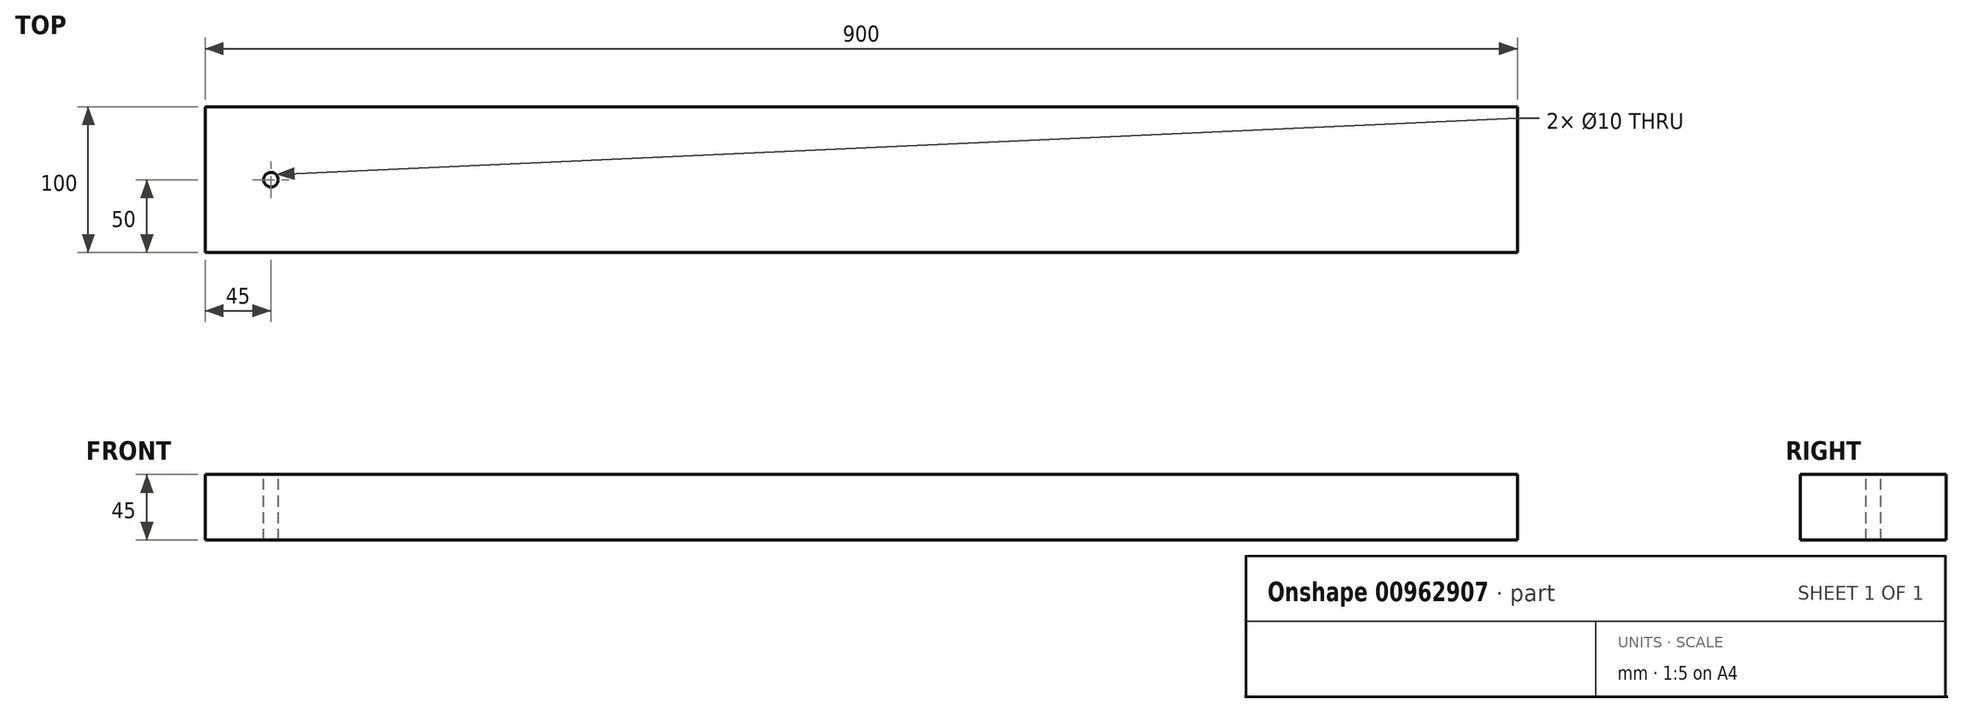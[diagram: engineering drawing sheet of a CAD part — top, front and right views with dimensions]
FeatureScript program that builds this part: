
annotation { "Feature Type Name" : "Feature", "Feature Type Description" : "" }
export const myFeature = defineFeature(function(context is Context, id is Id, definition is map)
    precondition{}
    {
        {
            var Q0;
            Q0=qCreatedBy(makeId("Top.planeOp"),FACE);
            var sketch = newSketch(context, id + "F0", { "sketchPlane" : qUnion([Q0])});
            skLineSegment(sketch, "E0.bottom", {"start": v(-450, 50) * mm, "end": v(450, 50) * mm});
            skLineSegment(sketch, "E0.top", {"start": v(-450, -50) * mm, "end": v(450, -50) * mm});
            skLineSegment(sketch, "E0.left", {"start": v(-450, 50) * mm, "end": v(-450, -50) * mm});
            skLineSegment(sketch, "E0.right", {"start": v(450, 50) * mm, "end": v(450, -50) * mm});
            skPoint(sketch, "E0.middle", {"position": v(0, 0) * mm});
            skSolve(sketch);
        }
        {
            var Q0;
            Q0 = qSketchRegion(id + "F0", true);
            extrude(context, id + "F1", {"entities" : qUnion([Q0]), "depth" : 45 * mm, "offsetDistance" : 25 * mm});
        }
        {
            var Q0;
            Q0=makeQuery(id+"F1.opExtrude","CAP_FACE",FACE,{"disambiguationData":[OSD([sQuery(id+"F0.wireOp",EDGE,"E0.bottom"),sQuery(id+"F0.wireOp",EDGE,"E0.top"),sQuery(id+"F0.wireOp",EDGE,"E0.left"),sQuery(id+"F0.wireOp",EDGE,"E0.right")])],"isStart":false});
            var sketch = newSketch(context, id + "F2", { "sketchPlane" : qUnion([Q0])});
            skLineSegment(sketch, "E1", {"start": v(-450, 0) * mm, "end": v(-405, 0) * mm});
            skLineSegment(sketch, "E2", {"start": v(-450, 50) * mm, "end": v(-450, 0) * mm});
            skLineSegment(sketch, "E3", {"start": v(-450, 0) * mm, "end": v(-450, -50) * mm});
            skCircle(sketch, "E4", {"center": v(-405, 0) * mm, "radius": 5 * mm});
            skSolve(sketch);
        }
        {
            var Q0;
            Q0 = qSketchRegion(id + "F2", true);
            extrude(context, id + "F3", {"entities" : qUnion([Q0]), "operationType" : NewBodyOperationType.REMOVE, "oppositeDirection" : true, "depth" : 130.1 * mm, "offsetDistance" : 25 * mm});
        }
    });
